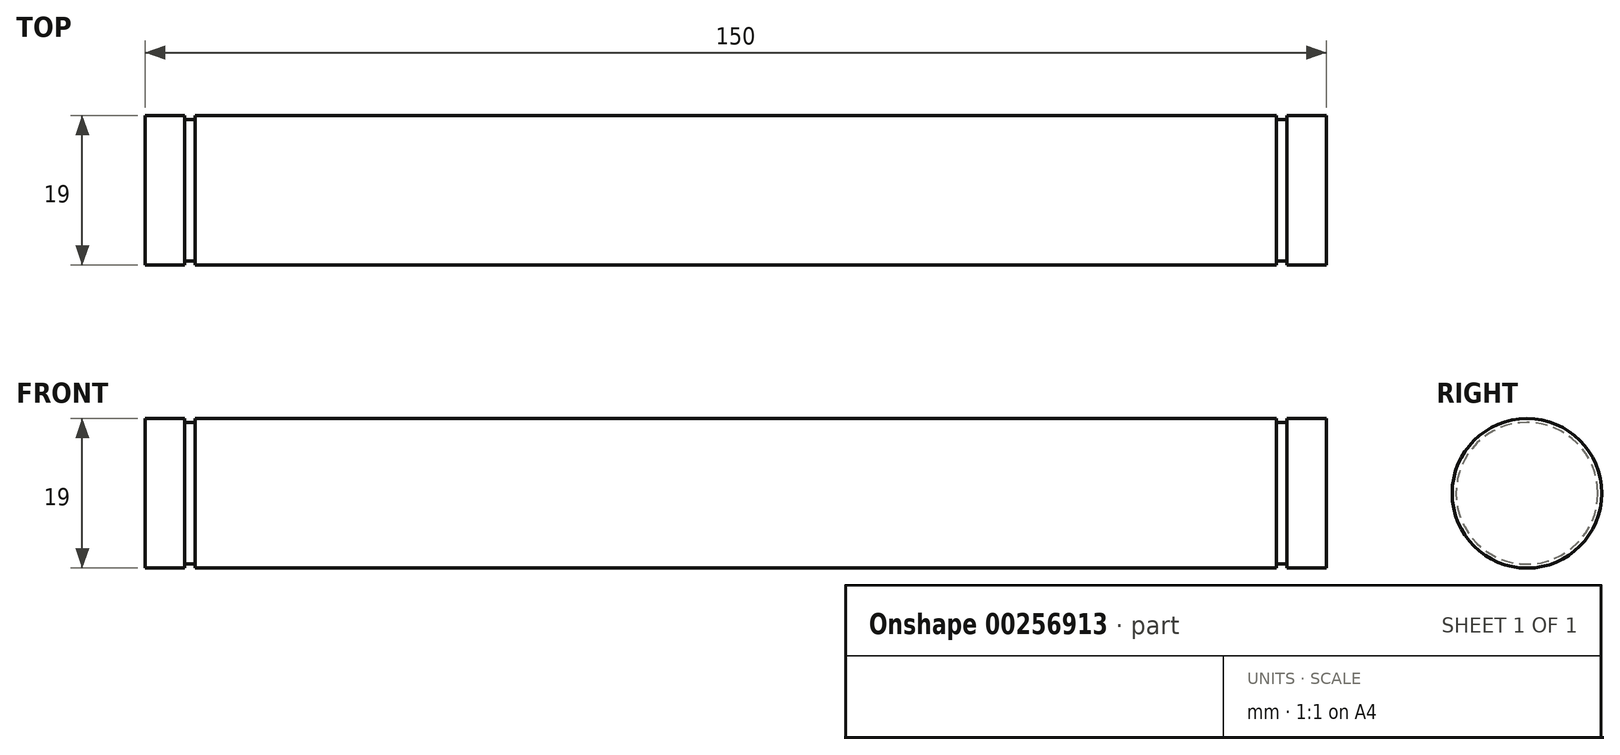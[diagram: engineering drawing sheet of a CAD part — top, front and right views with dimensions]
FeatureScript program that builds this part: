
annotation { "Feature Type Name" : "Feature", "Feature Type Description" : "" }
export const myFeature = defineFeature(function(context is Context, id is Id, definition is map)
    precondition{}
    {
        {
            var Q0;
            Q0=qCreatedBy(makeId("Right.planeOp"),FACE);
            var sketch = newSketch(context, id + "F0", { "sketchPlane" : qUnion([Q0])});
            skCircle(sketch, "E0", {"center": v(0, 0) * mm, "radius": 9.5 * mm});
            skSolve(sketch);
        }
        {
            var Q0;
            Q0=makeQuery(id+"F0.imprint","IMPRINT",FACE,{"disambiguationData":[TD([[makeQuery(id+"F0.imprint","IMPRINT",EDGE,{"derivedFrom":sQuery(id+"F0.wireOp",EDGE,"E0")}),1.0]])]});
            extrude(context, id + "F1", {"entities" : qUnion([Q0]), "oppositeDirection" : true, "depth" : 150 * mm});
        }
        {
            var Q0;
            Q0=qCreatedBy(makeId("Front.planeOp"),FACE);
            var sketch = newSketch(context, id + "F2", { "sketchPlane" : qUnion([Q0])});
            skLineSegment(sketch, "E1.bottom", {"start": v(-5, 9.5) * mm, "end": v(-6.3, 9.5) * mm});
            skLineSegment(sketch, "E1.top", {"start": v(-5, 9) * mm, "end": v(-6.3, 9) * mm});
            skLineSegment(sketch, "E1.left", {"start": v(-5, 9.5) * mm, "end": v(-5, 9) * mm});
            skLineSegment(sketch, "E1.right", {"start": v(-6.3, 9.5) * mm, "end": v(-6.3, 9) * mm});
            skLineSegment(sketch, "E2", {"start": v(0, 0) * mm, "end": v(-150, 0) * mm, "construction": true});
            skLineSegment(sketch, "E3", {"start": v(-75, 0) * mm, "end": v(-75, 18.44) * mm, "construction": true});
            skPoint(sketch, "E3.endSnap0", {"position": v(-75, 0) * mm});
            skLineSegment(sketch, "E4.MirrorCS", {"start": v(-143.7, 9.5) * mm, "end": v(-143.7, 9) * mm});
            skLineSegment(sketch, "E5.MirrorCS", {"start": v(-145, 9.5) * mm, "end": v(-145, 9) * mm});
            skLineSegment(sketch, "E6.MirrorCS", {"start": v(-145, 9.5) * mm, "end": v(-143.7, 9.5) * mm});
            skLineSegment(sketch, "E7.MirrorCS", {"start": v(-145, 9) * mm, "end": v(-143.7, 9) * mm});
            skSolve(sketch);
        }
        {
            var Q0;
            Q0 = qSketchRegion(id + "F2", true);
            var Q1;
            Q1=sQuery(id+"F2.wireOp",EDGE,"E2");
            revolve(context, id + "F3", {"operationType" : NewBodyOperationType.REMOVE, "entities" : qUnion([Q0]), "axis" : qUnion([Q1]), "revolveType" : RevolveType.FULL, "oppositeDirection" : true});
        }
    });
